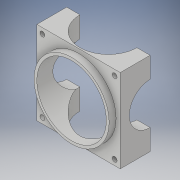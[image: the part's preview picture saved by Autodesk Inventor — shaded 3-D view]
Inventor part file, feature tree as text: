
AUTODESK INVENTOR PART (.ipt)
format: ipt  version: 2019 (Build 230136000, 136)  size: 204,800 bytes
history: native  units: mm
features: extrude x7, sketch x7, projected_geometry x5, pattern_circular x1
ambient origin geometry x8: Origin, YZ Plane, XZ Plane, XY Plane, X Axis, Y Axis, Z Axis, Center Point
bodies: Solid1 (feature_tree)
feature tree (20):
  extrude  "Extrusion1"  Depth=60.0mm
  extrude  "Extrusion2"  Depth=50.0mm
  extrude  "Extrusion3"  Depth=30.0mm
  extrude  "Extrusion4"  Depth=21.5mm
  extrude  "Extrusion5"  Depth=43.0mm
  extrude  "Extrusion6"  Depth=41.0mm
  pattern_circular  "Circular Pattern1"  Count=6  [1 undecoded]
  extrude  "Extrusion7"  Depth=21.5mm
  sketch  "Sketch1"  dims[d0=60.0mm d1=60.0mm]
  sketch  "Sketch2"  dims[d2=43.0mm d3=0.0mm d4=50.0mm]
  sketch  "Sketch3"  dims[d5=43.0mm d6=0.0mm d7=30.0mm]
  projected_geometry  "Projected Loop1"
  sketch  "Sketch4"  dims[d8=21.5mm d9=30.0mm]
  projected_geometry  "Projected Loop2"
  sketch  "Sketch5"  dims[d10=60.0mm d11=43.0mm]
  projected_geometry  "Projected Loop3"
  sketch  "Sketch6"  dims[d12=430.0mm d13=0.0mm d14=41.0mm d15=60.0mm]
  projected_geometry  "Projected Loop4"
  sketch  "Sketch7"  dims[d16=43.0mm d17=21.5mm d18=30.0mm d19=430.0mm d20=0.0mm d21=2.0mm d22=5.0mm d23=0.0mm d24=3.5mm d25=4.0mm d26=4.0mm d27=500.0mm d28=0.0mm d29=40.0mm d30=360.0deg d32=21.5mm d33=0.0mm]
  projected_geometry  "Projected Loop5"
note: 1 required parameter value undecoded (feature->parameter linkage not recoverable at this tier; creation-order binding heuristic only, values carry confidence <= 0.55)
